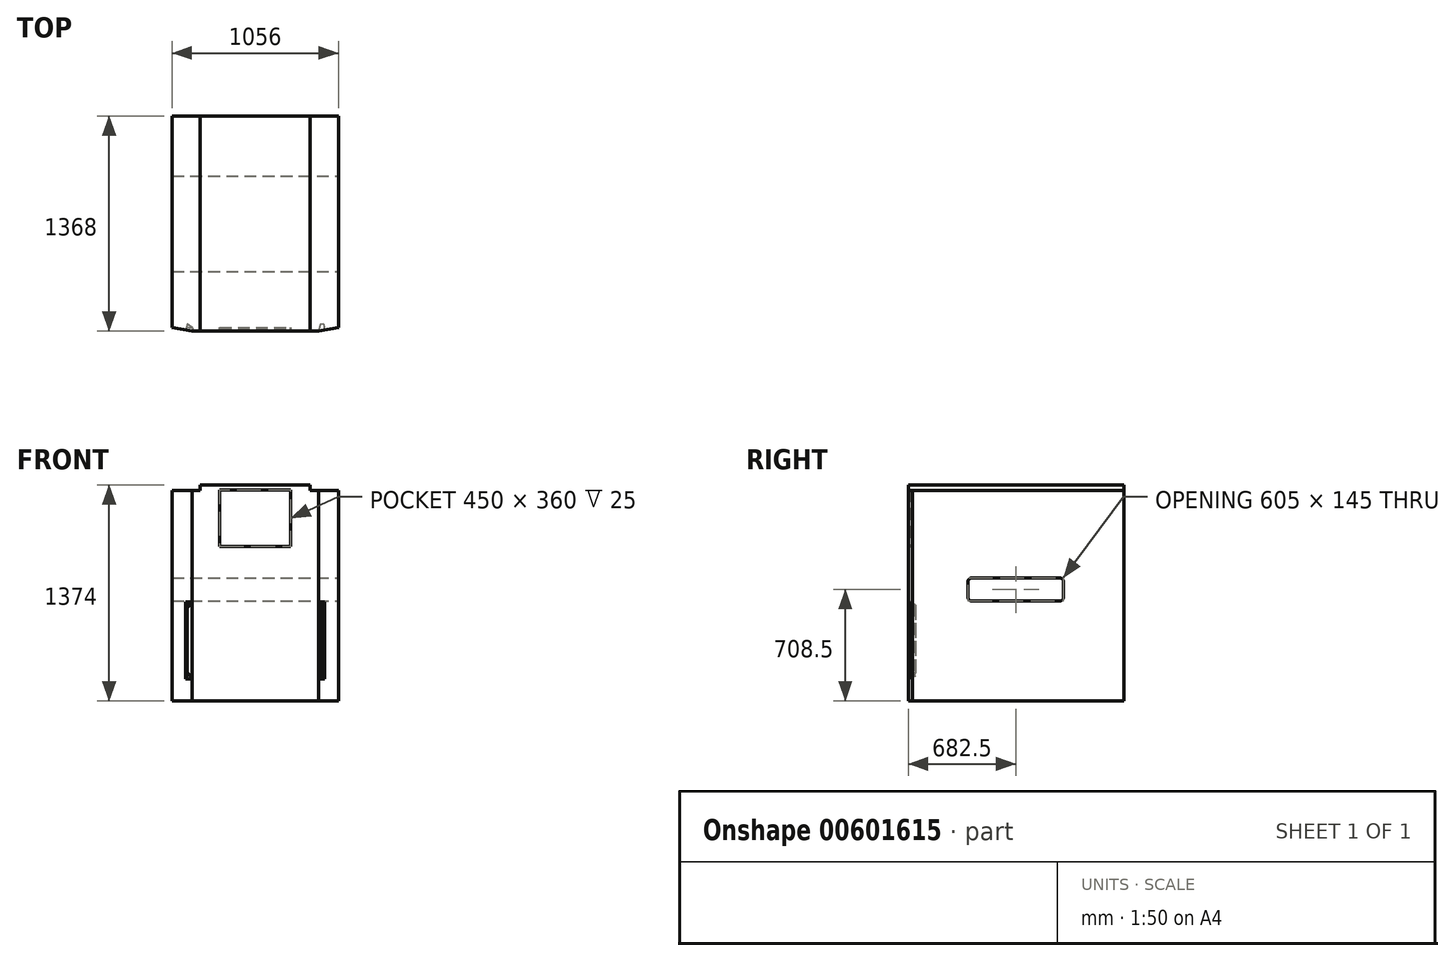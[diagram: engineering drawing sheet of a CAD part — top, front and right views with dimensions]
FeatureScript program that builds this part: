
annotation { "Feature Type Name" : "Feature", "Feature Type Description" : "" }
export const myFeature = defineFeature(function(context is Context, id is Id, definition is map)
    precondition{}
    {
        {
            var Q0;
            Q0=qCreatedBy(makeId("Top.planeOp"),FACE);
            var sketch = newSketch(context, id + "F0", { "sketchPlane" : qUnion([Q0])});
            skLineSegment(sketch, "E0", {"start": v(0, 1368) * mm, "end": v(0, 25) * mm});
            skLineSegment(sketch, "E1", {"start": v(0, 25) * mm, "end": v(126.5, 0) * mm});
            skLineSegment(sketch, "E2", {"start": v(126.5, 0) * mm, "end": v(929.5, 0) * mm});
            skLineSegment(sketch, "E3", {"start": v(929.5, 0) * mm, "end": v(1056, 25) * mm});
            skLineSegment(sketch, "E4", {"start": v(1056, 25) * mm, "end": v(1056, 1368) * mm});
            skLineSegment(sketch, "E5", {"start": v(1056, 1368) * mm, "end": v(0, 1368) * mm});
            skSolve(sketch);
        }
        {
            var Q0;
            Q0=makeQuery(id+"F0.imprint","IMPRINT",FACE,{"disambiguationData":[TD([[makeQuery(id+"F0.imprint","IMPRINT",EDGE,{"derivedFrom":sQuery(id+"F0.wireOp",EDGE,"E0")}),1.0]])]});
            extrude(context, id + "F1", {"entities" : qUnion([Q0]), "depth" : 1338 * mm, "offsetDistance" : 25 * mm});
        }
        {
            var Q0;
            Q0=makeQuery(id+"F1.opExtrude","CAP_FACE",FACE,{"disambiguationData":[OSD([sQuery(id+"F0.wireOp",EDGE,"E0"),sQuery(id+"F0.wireOp",EDGE,"E1"),sQuery(id+"F0.wireOp",EDGE,"E2"),sQuery(id+"F0.wireOp",EDGE,"E3"),sQuery(id+"F0.wireOp",EDGE,"E4"),sQuery(id+"F0.wireOp",EDGE,"E5")])],"isStart":false});
            var sketch = newSketch(context, id + "F2", { "sketchPlane" : qUnion([Q0])});
            skLineSegment(sketch, "E6.bottom", {"start": v(0, 190) * mm, "end": v(1057.9, 190) * mm});
            skLineSegment(sketch, "E6.top", {"start": v(0, 0) * mm, "end": v(1057.9, 0) * mm});
            skLineSegment(sketch, "E6.left", {"start": v(0, 190) * mm, "end": v(0, 0) * mm});
            skLineSegment(sketch, "E6.right", {"start": v(1057.9, 190) * mm, "end": v(1057.9, 0) * mm});
            skSolve(sketch);
        }
        {
            var Q0;
            {var subQ0=makeQuery(id+"F1.opExtrude","CAP_EDGE",EDGE,{"disambiguationData":[OSD([sQuery(id+"F0.wireOp",EDGE,"E1")])],"isStart":false});Q0=makeQuery(id+"F2.imprint","IMPRINT",FACE,{"disambiguationData":[TD([[makeQuery(id+"F2.imprint","IMPRINT",EDGE,{"derivedFrom":subQ0}),1.0]])]});}
            extrude(context, id + "F3", {"entities" : qUnion([Q0]), "operationType" : NewBodyOperationType.REMOVE, "oppositeDirection" : true, "depth" : 642 * mm, "offsetDistance" : 25 * mm});
        }
        {
            var Q0;
            Q0=makeQuery(id+"F3.boolean.opBoolean","COPY",FACE,{"derivedFrom":makeQuery(id+"F3.opExtrude","CAP_FACE",FACE,{"disambiguationData":[OSD([sQuery(id+"F0.wireOp",EDGE,"E1"),sQuery(id+"F0.wireOp",EDGE,"E3"),sQuery(id+"F0.wireOp",EDGE,"E4"),sQuery(id+"F2.wireOp",EDGE,"E6.bottom"),sQuery(id+"F2.wireOp",EDGE,"E6.top"),sQuery(id+"F2.wireOp",EDGE,"E6.left")])],"isStart":false})});
            extrude(context, id + "F4", {"entities" : qUnion([Q0]), "depth" : 215 * mm, "offsetDistance" : 25 * mm});
        }
        {
            var Q0;
            Q0=makeQuery(id+"F4.opExtrude","CAP_FACE",FACE,{"disambiguationData":[OSD([sQuery(id+"F0.wireOp",EDGE,"E1"),sQuery(id+"F0.wireOp",EDGE,"E3"),sQuery(id+"F0.wireOp",EDGE,"E4"),sQuery(id+"F2.wireOp",EDGE,"E6.bottom"),sQuery(id+"F2.wireOp",EDGE,"E6.top"),sQuery(id+"F2.wireOp",EDGE,"E6.left")])],"isStart":false});
            var sketch = newSketch(context, id + "F5", { "sketchPlane" : qUnion([Q0])});
            skLineSegment(sketch, "E7.bottom", {"start": v(178, 0) * mm, "end": v(878, 0) * mm});
            skLineSegment(sketch, "E7.top", {"start": v(178, 190) * mm, "end": v(878, 190) * mm});
            skLineSegment(sketch, "E7.left", {"start": v(178, 0) * mm, "end": v(178, 190) * mm});
            skLineSegment(sketch, "E7.right", {"start": v(878, 0) * mm, "end": v(878, 190) * mm});
            skSolve(sketch);
        }
        {
            var Q0;
            Q0=makeQuery(id+"F5.imprint","IMPRINT",FACE,{"disambiguationData":[TD([[makeQuery(id+"F5.imprint","IMPRINT",EDGE,{"derivedFrom":sQuery(id+"F5.wireOp",EDGE,"E7.bottom")}),1.0]])]});
            extrude(context, id + "F6", {"entities" : qUnion([Q0]), "depth" : 463 * mm, "offsetDistance" : 25 * mm});
        }
        {
            var Q0;
            Q0=makeQuery(id+"F4.opExtrude","CAP_FACE",FACE,{"disambiguationData":[OSD([sQuery(id+"F0.wireOp",EDGE,"E1"),sQuery(id+"F0.wireOp",EDGE,"E3"),sQuery(id+"F0.wireOp",EDGE,"E4"),sQuery(id+"F2.wireOp",EDGE,"E6.bottom"),sQuery(id+"F2.wireOp",EDGE,"E6.top"),sQuery(id+"F2.wireOp",EDGE,"E6.left")])],"isStart":false});
            var sketch = newSketch(context, id + "F7", { "sketchPlane" : qUnion([Q0])});
            skLineSegment(sketch, "E8.bottom", {"start": v(0, 0) * mm, "end": v(178, 0) * mm});
            skLineSegment(sketch, "E8.top", {"start": v(0, 190) * mm, "end": v(178, 190) * mm});
            skLineSegment(sketch, "E8.left", {"start": v(0, 0) * mm, "end": v(0, 190) * mm});
            skLineSegment(sketch, "E8.right", {"start": v(178, 0) * mm, "end": v(178, 190) * mm});
            skLineSegment(sketch, "E9.bottom", {"start": v(1056, 190) * mm, "end": v(878, 190) * mm});
            skLineSegment(sketch, "E9.top", {"start": v(1056, 0) * mm, "end": v(878, 0) * mm});
            skLineSegment(sketch, "E9.left", {"start": v(1056, 190) * mm, "end": v(1056, 0) * mm});
            skLineSegment(sketch, "E9.right", {"start": v(878, 190) * mm, "end": v(878, 0) * mm});
            skSolve(sketch);
        }
        {
            var Q0;
            {var subQ2=sQuery(id+"F7.wireOp",EDGE,"E8.top");Q0=makeQuery(id+"F7.imprint","IMPRINT",FACE,{"disambiguationData":[TD([[makeQuery(id+"F7.imprint","IMPRINT",EDGE,{"derivedFrom":subQ2}),-1.0]])]});}
            var Q1;
            {var subQ2=sQuery(id+"F7.wireOp",EDGE,"E9.bottom");Q1=makeQuery(id+"F7.imprint","IMPRINT",FACE,{"disambiguationData":[TD([[makeQuery(id+"F7.imprint","IMPRINT",EDGE,{"derivedFrom":subQ2}),-1.0]])]});}
            var Q2;
            Q2=makeQuery(id+"F1.opExtrude","CAP_FACE",FACE,{"disambiguationData":[OSD([sQuery(id+"F0.wireOp",EDGE,"E0"),sQuery(id+"F0.wireOp",EDGE,"E1"),sQuery(id+"F0.wireOp",EDGE,"E2"),sQuery(id+"F0.wireOp",EDGE,"E3"),sQuery(id+"F0.wireOp",EDGE,"E4"),sQuery(id+"F0.wireOp",EDGE,"E5")])],"isStart":false});
            extrude(context, id + "F8", {"entities" : qUnion([Q0, Q1]), "operationType" : NewBodyOperationType.ADD, "endBound" : BoundingType.UP_TO_SURFACE, "depth" : 25 * mm, "endBoundEntityFace" : qUnion([Q2]), "offsetDistance" : 25 * mm});
        }
        {
            var Q0;
            Q0=makeQuery(id+"F6.opExtrude","SWEPT_FACE",FACE,{"disambiguationData":[OSD([sQuery(id+"F5.wireOp",EDGE,"E7.top")])]});
            var sketch = newSketch(context, id + "F9", { "sketchPlane" : qUnion([Q0])});
            skLineSegment(sketch, "E10.bottom", {"start": v(-878, 1374) * mm, "end": v(-178, 1374) * mm});
            skLineSegment(sketch, "E10.top", {"start": v(-878, 1338) * mm, "end": v(-178, 1338) * mm});
            skLineSegment(sketch, "E10.left", {"start": v(-878, 1374) * mm, "end": v(-878, 1338) * mm});
            skLineSegment(sketch, "E10.right", {"start": v(-178, 1374) * mm, "end": v(-178, 1338) * mm});
            skSolve(sketch);
        }
        {
            var Q0;
            Q0=makeQuery(id+"F9.imprint","IMPRINT",FACE,{"disambiguationData":[TD([[makeQuery(id+"F9.imprint","IMPRINT",EDGE,{"derivedFrom":sQuery(id+"F9.wireOp",EDGE,"E10.bottom")}),1.0]])]});
            var Q1;
            Q1=makeQuery(id+"F1.opExtrude","SWEPT_FACE",FACE,{"disambiguationData":[OSD([sQuery(id+"F0.wireOp",EDGE,"E5")])]});
            extrude(context, id + "F10", {"entities" : qUnion([Q0]), "operationType" : NewBodyOperationType.ADD, "endBound" : BoundingType.UP_TO_SURFACE, "depth" : 25 * mm, "endBoundEntityFace" : qUnion([Q1]), "offsetDistance" : 25 * mm});
        }
        {
            var Q0;
            Q0=makeQuery(id+"F8.boolean.opBoolean","MERGE",FACE,{"derivedFrom":[makeQuery(id+"F1.opExtrude","SWEPT_FACE",FACE,{"disambiguationData":[OSD([sQuery(id+"F0.wireOp",EDGE,"E4")])]}),makeQuery(id+"F8.opExtrude","SWEPT_FACE",FACE,{"disambiguationData":[OSD([sQuery(id+"F7.wireOp",EDGE,"E9.left")])]})]});
            var sketch = newSketch(context, id + "F11", { "sketchPlane" : qUnion([Q0])});
            skLineSegment(sketch, "E11.bottom", {"start": v(380, 781) * mm, "end": v(985, 781) * mm});
            skLineSegment(sketch, "E11.top", {"start": v(380, 636) * mm, "end": v(985, 636) * mm});
            skLineSegment(sketch, "E11.left", {"start": v(380, 781) * mm, "end": v(380, 636) * mm});
            skLineSegment(sketch, "E11.right", {"start": v(985, 781) * mm, "end": v(985, 636) * mm});
            skSolve(sketch);
        }
        {
            var Q0;
            Q0=makeQuery(id+"F11.imprint","IMPRINT",FACE,{"disambiguationData":[TD([[makeQuery(id+"F11.imprint","IMPRINT",EDGE,{"derivedFrom":sQuery(id+"F11.wireOp",EDGE,"E11.bottom")}),-1.0]])]});
            extrude(context, id + "F12", {"entities" : qUnion([Q0]), "operationType" : NewBodyOperationType.REMOVE, "endBound" : BoundingType.THROUGH_ALL, "oppositeDirection" : true, "depth" : 25 * mm, "offsetDistance" : 25 * mm});
        }
        {
            var Q0;
            Q0=makeQuery(id+"F12.boolean.opBoolean","COPY",EDGE,{"derivedFrom":makeQuery(id+"F12.opExtrude","SWEPT_EDGE",EDGE,{"disambiguationData":[OSD([sQuery(id+"F11.wireOp",EDGE,"E11.bottom"),sQuery(id+"F11.wireOp",EDGE,"E11.left")])]})});
            var Q1;
            Q1=makeQuery(id+"F12.boolean.opBoolean","COPY",EDGE,{"derivedFrom":makeQuery(id+"F12.opExtrude","SWEPT_EDGE",EDGE,{"disambiguationData":[OSD([sQuery(id+"F11.wireOp",EDGE,"E11.bottom"),sQuery(id+"F11.wireOp",EDGE,"E11.right")])]})});
            var Q2;
            Q2=makeQuery(id+"F12.boolean.opBoolean","COPY",EDGE,{"derivedFrom":makeQuery(id+"F12.opExtrude","SWEPT_EDGE",EDGE,{"disambiguationData":[OSD([sQuery(id+"F11.wireOp",EDGE,"E11.top"),sQuery(id+"F11.wireOp",EDGE,"E11.left")])]})});
            var Q3;
            Q3=makeQuery(id+"F12.boolean.opBoolean","COPY",EDGE,{"derivedFrom":makeQuery(id+"F12.opExtrude","SWEPT_EDGE",EDGE,{"disambiguationData":[OSD([sQuery(id+"F11.wireOp",EDGE,"E11.top"),sQuery(id+"F11.wireOp",EDGE,"E11.right")])]})});
            fillet(context, id + "F13", {"entities" : qUnion([Q0, Q1, Q2, Q3]), "radius" : 20 * mm, "tangentPropagation" : true, "allowEdgeOverflow" : false});
        }
        {
            var Q0;
            Q0=makeQuery(id+"F6.opExtrude","SWEPT_FACE",FACE,{"disambiguationData":[OSD([sQuery(id+"F5.wireOp",EDGE,"E7.bottom")])]});
            var sketch = newSketch(context, id + "F14", { "sketchPlane" : qUnion([Q0])});
            skLineSegment(sketch, "E12.bottom", {"start": v(303, 1341) * mm, "end": v(753, 1341) * mm});
            skLineSegment(sketch, "E12.top", {"start": v(303, 981) * mm, "end": v(753, 981) * mm});
            skLineSegment(sketch, "E12.left", {"start": v(303, 1341) * mm, "end": v(303, 981) * mm});
            skLineSegment(sketch, "E12.right", {"start": v(753, 1341) * mm, "end": v(753, 981) * mm});
            skSolve(sketch);
        }
        {
            var Q0;
            Q0=makeQuery(id+"F14.imprint","IMPRINT",FACE,{"disambiguationData":[TD([[makeQuery(id+"F14.imprint","IMPRINT",EDGE,{"derivedFrom":sQuery(id+"F14.wireOp",EDGE,"E12.bottom")}),-1.0]])]});
            extrude(context, id + "F15", {"entities" : qUnion([Q0]), "operationType" : NewBodyOperationType.REMOVE, "oppositeDirection" : true, "depth" : 25 * mm, "offsetDistance" : 25 * mm});
        }
        {
            var Q0;
            Q0=makeQuery(id+"F15.boolean.opBoolean","COPY",FACE,{"derivedFrom":makeQuery(id+"F15.opExtrude","CAP_FACE",FACE,{"disambiguationData":[OSD([sQuery(id+"F14.wireOp",EDGE,"E12.bottom"),sQuery(id+"F14.wireOp",EDGE,"E12.top"),sQuery(id+"F14.wireOp",EDGE,"E12.left"),sQuery(id+"F14.wireOp",EDGE,"E12.right")])],"isStart":false})});
            extrude(context, id + "F16", {"entities" : qUnion([Q0]), "depth" : 10 * mm, "offsetDistance" : 25 * mm});
        }
        {
            var Q0;
            Q0=makeQuery(id+"F1.opExtrude","SWEPT_FACE",FACE,{"disambiguationData":[OSD([sQuery(id+"F0.wireOp",EDGE,"E1")])]});
            var sketch = newSketch(context, id + "F17", { "sketchPlane" : qUnion([Q0])});
            skLineSegment(sketch, "E13.bottom", {"start": v(124.1, 631) * mm, "end": v(84.1, 631) * mm});
            skLineSegment(sketch, "E13.top", {"start": v(124.1, 141) * mm, "end": v(84.1, 141) * mm});
            skLineSegment(sketch, "E13.left", {"start": v(124.1, 631) * mm, "end": v(124.1, 141) * mm});
            skLineSegment(sketch, "E13.right", {"start": v(84.1, 631) * mm, "end": v(84.1, 141) * mm});
            skSolve(sketch);
        }
        {
            var Q0;
            Q0=makeQuery(id+"F17.imprint","IMPRINT",FACE,{"disambiguationData":[TD([[makeQuery(id+"F17.imprint","IMPRINT",EDGE,{"derivedFrom":sQuery(id+"F17.wireOp",EDGE,"E13.bottom")}),1.0]])]});
            extrude(context, id + "F18", {"entities" : qUnion([Q0]), "operationType" : NewBodyOperationType.REMOVE, "oppositeDirection" : true, "depth" : 40 * mm, "offsetDistance" : 25 * mm});
        }
        {
            var Q0;
            Q0=makeQuery(id+"F18.boolean.opBoolean","COPY",EDGE,{"derivedFrom":makeQuery(id+"F18.opExtrude","CAP_EDGE",EDGE,{"disambiguationData":[OSD([sQuery(id+"F17.wireOp",EDGE,"E13.left")])],"isStart":false})});
            var Q1;
            Q1=makeQuery(id+"F18.boolean.opBoolean","COPY",EDGE,{"derivedFrom":makeQuery(id+"F18.opExtrude","CAP_EDGE",EDGE,{"disambiguationData":[OSD([sQuery(id+"F17.wireOp",EDGE,"E13.bottom")])],"isStart":false})});
            var Q2;
            Q2=makeQuery(id+"F18.boolean.opBoolean","COPY",EDGE,{"derivedFrom":makeQuery(id+"F18.opExtrude","CAP_EDGE",EDGE,{"disambiguationData":[OSD([sQuery(id+"F17.wireOp",EDGE,"E13.top")])],"isStart":false})});
            chamfer(context, id + "F19", {"entities" : qUnion([Q0, Q1, Q2]), "chamferType" : ChamferType.TWO_OFFSETS, "width1" : 40 * mm, "oppositeDirection" : false, "width2" : 20 * mm, "tangentPropagation" : true});
        }
        {
            var Q0;
            Q0=makeQuery(id+"F1.opExtrude","SWEPT_FACE",FACE,{"disambiguationData":[OSD([sQuery(id+"F0.wireOp",EDGE,"E3")])]});
            var sketch = newSketch(context, id + "F20", { "sketchPlane" : qUnion([Q0])});
            skLineSegment(sketch, "E14.bottom", {"start": v(911.86, 631) * mm, "end": v(951.86, 631) * mm});
            skLineSegment(sketch, "E14.top", {"start": v(911.86, 141) * mm, "end": v(951.86, 141) * mm});
            skLineSegment(sketch, "E14.left", {"start": v(911.86, 631) * mm, "end": v(911.86, 141) * mm});
            skLineSegment(sketch, "E14.right", {"start": v(951.86, 631) * mm, "end": v(951.86, 141) * mm});
            skSolve(sketch);
        }
        {
            var Q0;
            Q0=makeQuery(id+"F20.imprint","IMPRINT",FACE,{"disambiguationData":[TD([[makeQuery(id+"F20.imprint","IMPRINT",EDGE,{"derivedFrom":sQuery(id+"F20.wireOp",EDGE,"E14.bottom")}),-1.0]])]});
            extrude(context, id + "F21", {"entities" : qUnion([Q0]), "operationType" : NewBodyOperationType.REMOVE, "oppositeDirection" : true, "depth" : 40 * mm, "offsetDistance" : 25 * mm});
        }
        {
            var Q0;
            Q0=makeQuery(id+"F21.boolean.opBoolean","COPY",EDGE,{"derivedFrom":makeQuery(id+"F21.opExtrude","CAP_EDGE",EDGE,{"disambiguationData":[OSD([sQuery(id+"F20.wireOp",EDGE,"E14.left")])],"isStart":false})});
            var Q1;
            Q1=makeQuery(id+"F21.boolean.opBoolean","COPY",EDGE,{"derivedFrom":makeQuery(id+"F21.opExtrude","CAP_EDGE",EDGE,{"disambiguationData":[OSD([sQuery(id+"F20.wireOp",EDGE,"E14.bottom")])],"isStart":false})});
            var Q2;
            Q2=makeQuery(id+"F21.boolean.opBoolean","COPY",EDGE,{"derivedFrom":makeQuery(id+"F21.opExtrude","CAP_EDGE",EDGE,{"disambiguationData":[OSD([sQuery(id+"F20.wireOp",EDGE,"E14.top")])],"isStart":false})});
            chamfer(context, id + "F22", {"entities" : qUnion([Q0, Q1, Q2]), "chamferType" : ChamferType.TWO_OFFSETS, "width1" : 20 * mm, "oppositeDirection" : false, "width2" : 40 * mm, "tangentPropagation" : true});
        }
    });
